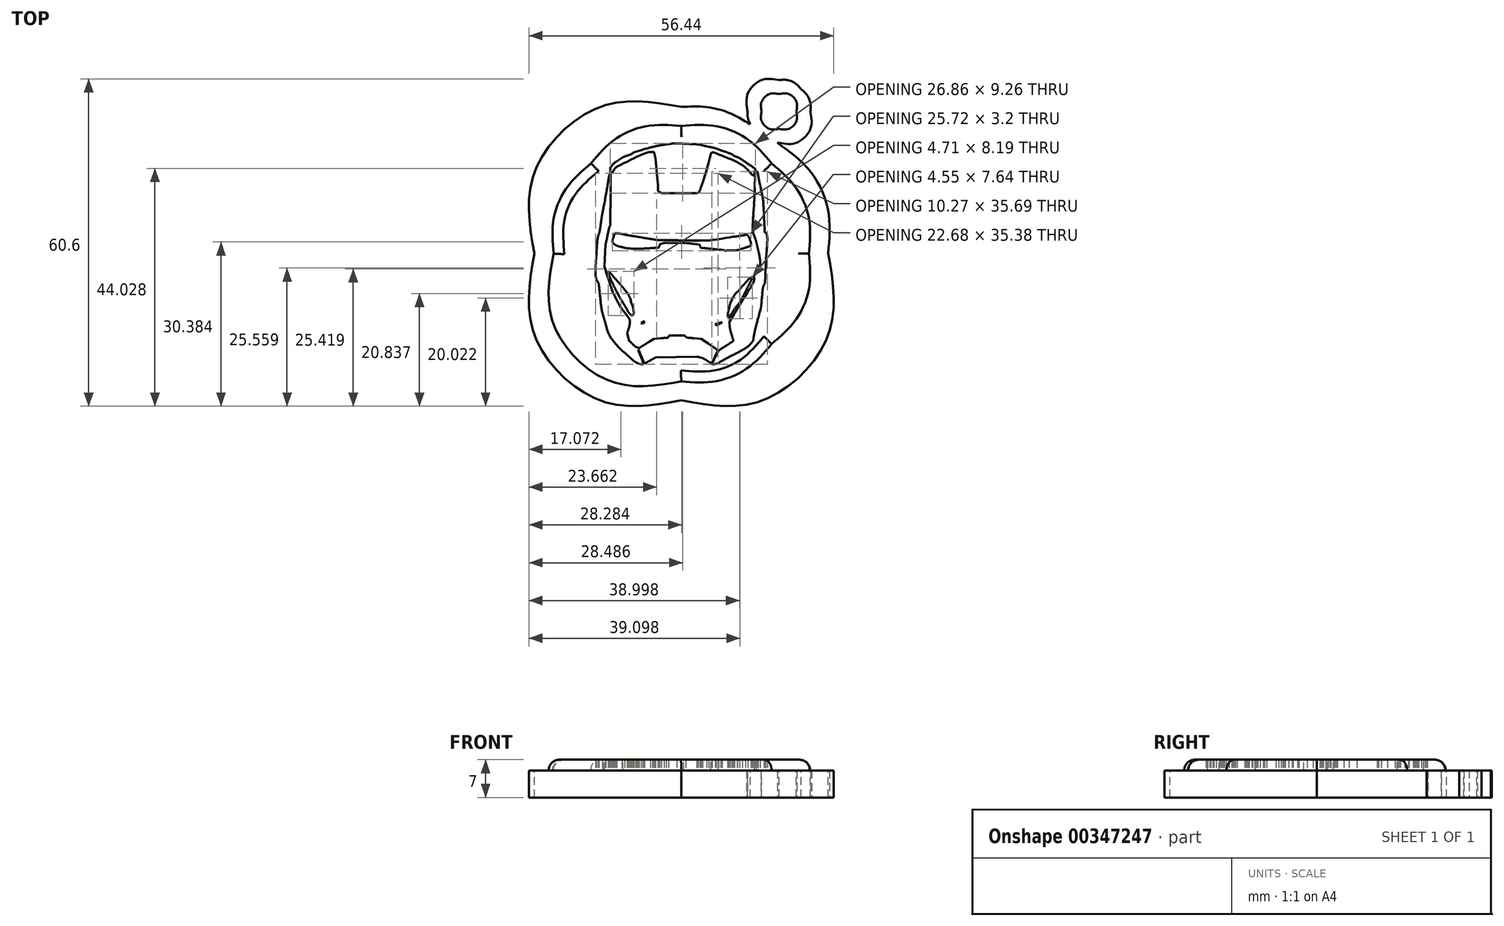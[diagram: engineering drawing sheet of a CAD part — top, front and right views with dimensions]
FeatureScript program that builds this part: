
annotation { "Feature Type Name" : "Feature", "Feature Type Description" : "" }
export const myFeature = defineFeature(function(context is Context, id is Id, definition is map)
    precondition{}
    {
        {
            var Q0;
            Q0=qCreatedBy(makeId("Top.planeOp"),FACE);
            var sketch = newSketch(context, id + "F0", { "sketchPlane" : qUnion([Q0])});
            skFitSpline(sketch, "E0", {"points": [v(-8.22, -22.7) * mm, v(-8.43, -22.6) * mm, v(-8.77, -22.38) * mm, v(-8.96, -22.21) * mm]});
            skFitSpline(sketch, "E1", {"points": [v(-8.96, -22.21) * mm, v(-9.15, -22.04) * mm, v(-9.54, -21.69) * mm, v(-9.83, -21.43) * mm]});
            skFitSpline(sketch, "E2", {"points": [v(-9.83, -21.43) * mm, v(-10.12, -21.17) * mm, v(-10.56, -20.8) * mm, v(-10.8, -20.6) * mm]});
            skFitSpline(sketch, "E3", {"points": [v(-10.8, -20.6) * mm, v(-11.06, -20.39) * mm, v(-11.61, -19.8) * mm, v(-12.04, -19.27) * mm]});
            skFitSpline(sketch, "E4", {"points": [v(-12.04, -19.27) * mm, v(-12.95, -18.16) * mm, v(-13.6, -16.93) * mm, v(-14, -15.53) * mm]});
            skFitSpline(sketch, "E5", {"points": [v(-14, -15.53) * mm, v(-14.14, -15.02) * mm, v(-14.36, -14.26) * mm, v(-14.48, -13.85) * mm]});
            skFitSpline(sketch, "E6", {"points": [v(-14.48, -13.85) * mm, v(-14.7, -13.05) * mm, v(-14.91, -11.53) * mm, v(-15.21, -8.5) * mm]});
            skFitSpline(sketch, "E7", {"points": [v(-15.21, -8.5) * mm, v(-15.23, -8.29) * mm, v(-15.34, -7.94) * mm, v(-15.45, -7.72) * mm]});
            skFitSpline(sketch, "E8", {"points": [v(-15.45, -7.72) * mm, v(-15.78, -7.08) * mm, v(-15.89, -5.4) * mm, v(-15.75, -3.2) * mm]});
            skFitSpline(sketch, "E9", {"points": [v(-15.75, -3.2) * mm, v(-15.59, -0.63) * mm, v(-15.46, 0.49) * mm, v(-15.26, 1.13) * mm]});
            skFitSpline(sketch, "E10", {"points": [v(-15.26, 1.13) * mm, v(-15.16, 1.44) * mm, v(-15, 2.32) * mm, v(-14.9, 3.1) * mm]});
            skFitSpline(sketch, "E11", {"points": [v(-14.9, 3.1) * mm, v(-14.79, 3.87) * mm, v(-14.66, 4.7) * mm, v(-14.6, 4.97) * mm]});
            skFitSpline(sketch, "E12", {"points": [v(-14.6, 4.97) * mm, v(-14.26, 6.74) * mm, v(-13.74, 9.57) * mm, v(-13.58, 10.63) * mm]});
            skFitSpline(sketch, "E13", {"points": [v(-13.58, 10.63) * mm, v(-13.47, 11.32) * mm, v(-13.35, 11.95) * mm, v(-13.32, 12.02) * mm]});
            skFitSpline(sketch, "E14", {"points": [v(-13.32, 12.02) * mm, v(-13.1, 12.44) * mm, v(-13.07, 11.84) * mm, v(-13.1, 7.5) * mm]});
            skFitSpline(sketch, "E15", {"points": [v(-13.1, 7.5) * mm, v(-13.12, 3.82) * mm, v(-13.16, 2.84) * mm, v(-13.27, 2.54) * mm]});
            skFitSpline(sketch, "E16", {"points": [v(-13.27, 2.54) * mm, v(-13.34, 2.33) * mm, v(-13.67, 0.81) * mm, v(-14, -0.83) * mm]});
            skFitSpline(sketch, "E17", {"points": [v(-14.24, -4.9) * mm, v(-14.04, -5.5) * mm, v(-13.61, -6.79) * mm, v(-13.3, -7.76) * mm]});
            skFitSpline(sketch, "E18", {"points": [v(-13.3, -7.76) * mm, v(-12.98, -8.74) * mm, v(-12.6, -9.77) * mm, v(-12.46, -10.06) * mm]});
            skFitSpline(sketch, "E19", {"points": [v(-12.46, -10.06) * mm, v(-11.7, -11.55) * mm, v(-11.06, -12.63) * mm, v(-10.45, -13.43) * mm]});
            skFitSpline(sketch, "E20", {"points": [v(-10.45, -13.43) * mm, v(-10.08, -13.92) * mm, v(-9.73, -14.4) * mm, v(-9.68, -14.5) * mm]});
            skFitSpline(sketch, "E21", {"points": [v(-9.68, -14.5) * mm, v(-9.52, -14.81) * mm, v(-9.71, -16.27) * mm, v(-10.03, -17.2) * mm]});
            skLineSegment(sketch, "E22", {"start": v(-14, -0.83) * mm, "end": v(-14.6, -3.82) * mm});
            skLineSegment(sketch, "E23", {"start": v(-14.6, -3.82) * mm, "end": v(-14.24, -4.9) * mm});
            skLineSegment(sketch, "E24", {"start": v(-14.24, -4.9) * mm, "end": v(-14, -0.83) * mm});
            skFitSpline(sketch, "E25", {"points": [v(-9.63, -18.65) * mm, v(-9.26, -19) * mm, v(-8.73, -19.48) * mm, v(-8.47, -19.74) * mm]});
            skLineSegment(sketch, "E26", {"start": v(-10.03, -17.2) * mm, "end": v(-10.32, -18.03) * mm});
            skLineSegment(sketch, "E27", {"start": v(-10.32, -18.03) * mm, "end": v(-9.63, -18.65) * mm});
            skLineSegment(sketch, "E28", {"start": v(-9.63, -18.65) * mm, "end": v(-10.03, -17.2) * mm});
            skFitSpline(sketch, "E29", {"points": [v(-7.78, -20) * mm, v(-7.66, -19.89) * mm, v(-7.37, -19.68) * mm, v(-7.13, -19.54) * mm]});
            skFitSpline(sketch, "E30", {"points": [v(-7.13, -19.54) * mm, v(-6.9, -19.4) * mm, v(-6.34, -19.06) * mm, v(-5.9, -18.78) * mm]});
            skLineSegment(sketch, "E31", {"start": v(-8.47, -19.74) * mm, "end": v(-8, -20.21) * mm});
            skLineSegment(sketch, "E32", {"start": v(-8, -20.21) * mm, "end": v(-7.78, -20) * mm});
            skLineSegment(sketch, "E33", {"start": v(-7.78, -20) * mm, "end": v(-8.47, -19.74) * mm});
            skFitSpline(sketch, "E34", {"points": [v(-3.8, -18.16) * mm, v(-2.63, -18.07) * mm, v(-2.5, -18.04) * mm, v(-2.37, -17.85) * mm]});
            skFitSpline(sketch, "E35", {"points": [v(-2.37, -17.85) * mm, v(-2.24, -17.65) * mm, v(-2.17, -17.64) * mm, v(-0.82, -17.64) * mm]});
            skFitSpline(sketch, "E36", {"points": [v(-0.82, -17.64) * mm, v(0.48, -17.64) * mm, v(0.6, -17.66) * mm, v(0.8, -17.84) * mm]});
            skFitSpline(sketch, "E37", {"points": [v(0.8, -17.84) * mm, v(0.97, -18) * mm, v(1.21, -18.05) * mm, v(2.35, -18.14) * mm]});
            skLineSegment(sketch, "E38", {"start": v(-5.9, -18.78) * mm, "end": v(-5.11, -18.26) * mm});
            skLineSegment(sketch, "E39", {"start": v(-5.11, -18.26) * mm, "end": v(-3.8, -18.16) * mm});
            skLineSegment(sketch, "E40", {"start": v(-3.8, -18.16) * mm, "end": v(-5.9, -18.78) * mm});
            skFitSpline(sketch, "E41", {"points": [v(4.95, -19.12) * mm, v(5.65, -19.59) * mm, v(6.34, -20.08) * mm, v(6.5, -20.2) * mm]});
            skLineSegment(sketch, "E42", {"start": v(2.35, -18.14) * mm, "end": v(3.7, -18.26) * mm});
            skLineSegment(sketch, "E43", {"start": v(3.7, -18.26) * mm, "end": v(4.95, -19.12) * mm});
            skLineSegment(sketch, "E44", {"start": v(4.95, -19.12) * mm, "end": v(2.35, -18.14) * mm});
            skFitSpline(sketch, "E45", {"points": [v(6.24, -21.52) * mm, v(5.94, -22.12) * mm, v(5.63, -22.63) * mm, v(5.56, -22.66) * mm]});
            skFitSpline(sketch, "E46", {"points": [v(5.56, -22.66) * mm, v(5.49, -22.7) * mm, v(5.1, -22.51) * mm, v(4.7, -22.27) * mm]});
            skFitSpline(sketch, "E47", {"points": [v(4.7, -22.27) * mm, v(4.13, -21.93) * mm, v(3.73, -21.77) * mm, v(2.85, -21.55) * mm]});
            skLineSegment(sketch, "E48", {"start": v(6.5, -20.2) * mm, "end": v(6.78, -20.43) * mm});
            skLineSegment(sketch, "E49", {"start": v(6.78, -20.43) * mm, "end": v(6.24, -21.52) * mm});
            skLineSegment(sketch, "E50", {"start": v(6.24, -21.52) * mm, "end": v(6.5, -20.2) * mm});
            skFitSpline(sketch, "E51", {"points": [v(-4.73, -21.7) * mm, v(-5.04, -21.87) * mm, v(-5.61, -22.18) * mm, v(-6, -22.4) * mm]});
            skFitSpline(sketch, "E52", {"points": [v(-6, -22.4) * mm, v(-6.38, -22.6) * mm, v(-6.74, -22.75) * mm, v(-6.8, -22.71) * mm]});
            skFitSpline(sketch, "E53", {"points": [v(-6.8, -22.71) * mm, v(-6.85, -22.68) * mm, v(-7, -22.42) * mm, v(-7.11, -22.13) * mm]});
            skFitSpline(sketch, "E54", {"points": [v(-7.11, -22.13) * mm, v(-7.53, -21.14) * mm, v(-7.9, -20.35) * mm, v(-7.93, -20.39) * mm]});
            skFitSpline(sketch, "E55", {"points": [v(-7.93, -20.39) * mm, v(-7.95, -20.4) * mm, v(-7.76, -20.94) * mm, v(-7.5, -21.57) * mm]});
            skFitSpline(sketch, "E56", {"points": [v(-7.5, -21.57) * mm, v(-7.24, -22.2) * mm, v(-7.03, -22.76) * mm, v(-7.03, -22.8) * mm]});
            skFitSpline(sketch, "E57", {"points": [v(-7.03, -22.8) * mm, v(-7.03, -22.95) * mm, v(-7.81, -22.88) * mm, v(-8.22, -22.7) * mm]});
            skLineSegment(sketch, "E58", {"start": v(2.85, -21.55) * mm, "end": v(1.73, -21.27) * mm});
            skLineSegment(sketch, "E59", {"start": v(1.73, -21.27) * mm, "end": v(-1.22, -21.34) * mm});
            skLineSegment(sketch, "E60", {"start": v(-1.22, -21.34) * mm, "end": v(-4.17, -21.4) * mm});
            skLineSegment(sketch, "E61", {"start": v(-4.17, -21.4) * mm, "end": v(-4.73, -21.7) * mm});
            skLineSegment(sketch, "E62", {"start": v(-4.73, -21.7) * mm, "end": v(2.85, -21.55) * mm});
            skFitSpline(sketch, "E63", {"points": [v(5.72, -22.81) * mm, v(5.88, -22.45) * mm, v(6.87, -20.56) * mm, v(6.95, -20.44) * mm]});
            skFitSpline(sketch, "E64", {"points": [v(6.95, -20.44) * mm, v(7.01, -20.37) * mm, v(7.59, -19.97) * mm, v(8.23, -19.56) * mm]});
            skFitSpline(sketch, "E65", {"points": [v(8.23, -19.56) * mm, v(8.87, -19.16) * mm, v(9.46, -18.77) * mm, v(9.52, -18.71) * mm]});
            skFitSpline(sketch, "E66", {"points": [v(9.52, -18.71) * mm, v(9.63, -18.62) * mm, v(9.6, -18.41) * mm, v(9.33, -17.54) * mm]});
            skFitSpline(sketch, "E67", {"points": [v(9.33, -17.54) * mm, v(9.15, -16.95) * mm, v(8.98, -16.17) * mm, v(8.95, -15.8) * mm]});
            skFitSpline(sketch, "E68", {"points": [v(9.78, -13.67) * mm, v(10.27, -12.85) * mm, v(11, -11.68) * mm, v(11.39, -11.05) * mm]});
            skFitSpline(sketch, "E69", {"points": [v(11.39, -11.05) * mm, v(12.53, -9.23) * mm, v(13.47, -7.38) * mm, v(13.47, -6.95) * mm]});
            skFitSpline(sketch, "E70", {"points": [v(13.47, -6.95) * mm, v(13.47, -6.67) * mm, v(13.61, -6.33) * mm, v(14.03, -5.57) * mm]});
            skFitSpline(sketch, "E71", {"points": [v(14.03, -5.57) * mm, v(14.42, -4.87) * mm, v(14.6, -4.46) * mm, v(14.6, -4.23) * mm]});
            skFitSpline(sketch, "E72", {"points": [v(14.6, -4.23) * mm, v(14.6, -3.9) * mm, v(14.38, -2.52) * mm, v(14.23, -1.87) * mm]});
            skFitSpline(sketch, "E73", {"points": [v(14.23, -1.87) * mm, v(14.18, -1.66) * mm, v(14.07, -1.18) * mm, v(13.98, -0.8) * mm]});
            skFitSpline(sketch, "E74", {"points": [v(13.98, -0.8) * mm, v(13.9, -0.4) * mm, v(13.72, 0.2) * mm, v(13.6, 0.57) * mm]});
            skFitSpline(sketch, "E75", {"points": [v(13.6, 0.57) * mm, v(13.27, 1.49) * mm, v(13.23, 2.84) * mm, v(13.43, 6.28) * mm]});
            skFitSpline(sketch, "E76", {"points": [v(13.43, 6.28) * mm, v(13.52, 7.82) * mm, v(13.6, 9.76) * mm, v(13.62, 10.58) * mm]});
            skFitSpline(sketch, "E77", {"points": [v(13.62, 10.58) * mm, v(13.64, 12.14) * mm, v(13.72, 12.62) * mm, v(13.95, 12.67) * mm]});
            skFitSpline(sketch, "E78", {"points": [v(13.95, 12.67) * mm, v(14.06, 12.69) * mm, v(14.2, 12.19) * mm, v(14.58, 10.23) * mm]});
            skFitSpline(sketch, "E79", {"points": [v(14.58, 10.23) * mm, v(15.08, 7.68) * mm, v(15.18, 6.84) * mm, v(15.35, 3.47) * mm]});
            skFitSpline(sketch, "E80", {"points": [v(15.35, 3.47) * mm, v(15.43, 1.84) * mm, v(15.47, 1.48) * mm, v(15.6, 1.33) * mm]});
            skFitSpline(sketch, "E81", {"points": [v(15.6, 1.33) * mm, v(15.82, 1.1) * mm, v(15.87, -0.9) * mm, v(15.72, -3) * mm]});
            skFitSpline(sketch, "E82", {"points": [v(15.72, -3) * mm, v(15.66, -3.81) * mm, v(15.6, -5.25) * mm, v(15.56, -6.17) * mm]});
            skFitSpline(sketch, "E83", {"points": [v(15.56, -6.17) * mm, v(15.51, -7.63) * mm, v(15.48, -7.91) * mm, v(15.3, -8.32) * mm]});
            skFitSpline(sketch, "E84", {"points": [v(15.3, -8.32) * mm, v(15.14, -8.69) * mm, v(15.05, -9.2) * mm, v(14.93, -10.53) * mm]});
            skFitSpline(sketch, "E85", {"points": [v(14.93, -10.53) * mm, v(14.77, -12.27) * mm, v(14.72, -12.52) * mm, v(14.27, -14.22) * mm]});
            skFitSpline(sketch, "E86", {"points": [v(14.27, -14.22) * mm, v(13.86, -15.73) * mm, v(13.58, -16.96) * mm, v(13.37, -18.1) * mm]});
            skFitSpline(sketch, "E87", {"points": [v(13.37, -18.1) * mm, v(13.29, -18.53) * mm, v(13.18, -18.79) * mm, v(12.98, -19.01) * mm]});
            skFitSpline(sketch, "E88", {"points": [v(12.98, -19.01) * mm, v(12.59, -19.46) * mm, v(11.16, -20.41) * mm, v(9.85, -21.1) * mm]});
            skFitSpline(sketch, "E89", {"points": [v(9.85, -21.1) * mm, v(9.24, -21.43) * mm, v(8.4, -21.87) * mm, v(8, -22.09) * mm]});
            skFitSpline(sketch, "E90", {"points": [v(8, -22.09) * mm, v(7.59, -22.3) * mm, v(7.08, -22.58) * mm, v(6.88, -22.69) * mm]});
            skFitSpline(sketch, "E91", {"points": [v(6.88, -22.69) * mm, v(6.52, -22.87) * mm, v(5.65, -22.97) * mm, v(5.72, -22.81) * mm]});
            skLineSegment(sketch, "E92", {"start": v(8.95, -15.8) * mm, "end": v(8.89, -15.14) * mm});
            skLineSegment(sketch, "E93", {"start": v(8.89, -15.14) * mm, "end": v(9.78, -13.67) * mm});
            skLineSegment(sketch, "E94", {"start": v(9.78, -13.67) * mm, "end": v(8.95, -15.8) * mm});
            skFitSpline(sketch, "E95", {"points": [v(5.7, -16.17) * mm, v(5.41, -15.87) * mm, v(5.07, -15.49) * mm, v(4.93, -15.31) * mm]});
            skFitSpline(sketch, "E96", {"points": [v(4.93, -15.31) * mm, v(4.77, -15.12) * mm, v(4.53, -14.96) * mm, v(4.32, -14.91) * mm]});
            skFitSpline(sketch, "E97", {"points": [v(4.32, -14.91) * mm, v(3.86, -14.8) * mm, v(-4.6, -14.64) * mm, v(-5.04, -14.74) * mm]});
            skFitSpline(sketch, "E98", {"points": [v(-5.04, -14.74) * mm, v(-5.31, -14.8) * mm, v(-5.55, -15) * mm, v(-6.17, -15.67) * mm]});
            skFitSpline(sketch, "E99", {"points": [v(-6.17, -15.67) * mm, v(-6.6, -16.14) * mm, v(-7.02, -16.52) * mm, v(-7.1, -16.52) * mm]});
            skFitSpline(sketch, "E100", {"points": [v(-7.1, -16.52) * mm, v(-7.2, -16.52) * mm, v(-7.6, -16.24) * mm, v(-8.01, -15.9) * mm]});
            skFitSpline(sketch, "E101", {"points": [v(-8.01, -15.9) * mm, v(-9.43, -14.71) * mm, v(-9.39, -14.76) * mm, v(-9.32, -14.45) * mm]});
            skFitSpline(sketch, "E102", {"points": [v(-9.32, -14.45) * mm, v(-9.28, -14.3) * mm, v(-9.2, -14.14) * mm, v(-9.12, -14.11) * mm]});
            skFitSpline(sketch, "E103", {"points": [v(-9.12, -14.11) * mm, v(-9.05, -14.08) * mm, v(-8.72, -14.28) * mm, v(-8.36, -14.57) * mm]});
            skFitSpline(sketch, "E104", {"points": [v(-8.36, -14.57) * mm, v(-8.01, -14.85) * mm, v(-7.6, -15.17) * mm, v(-7.43, -15.28) * mm]});
            skFitSpline(sketch, "E105", {"points": [v(-6.77, -15) * mm, v(-6.57, -14.73) * mm, v(-6.34, -14.39) * mm, v(-6.25, -14.25) * mm]});
            skFitSpline(sketch, "E106", {"points": [v(-6.25, -14.25) * mm, v(-5.88, -13.66) * mm, v(-6.02, -13.68) * mm, v(-1.47, -13.7) * mm]});
            skFitSpline(sketch, "E107", {"points": [v(-1.47, -13.7) * mm, v(2.96, -13.7) * mm, v(4.58, -13.76) * mm, v(4.95, -13.9) * mm]});
            skFitSpline(sketch, "E108", {"points": [v(4.95, -13.9) * mm, v(5.08, -13.96) * mm, v(5.39, -14.28) * mm, v(5.63, -14.63) * mm]});
            skFitSpline(sketch, "E109", {"points": [v(5.63, -14.63) * mm, v(5.88, -14.97) * mm, v(6.17, -15.37) * mm, v(6.29, -15.51) * mm]});
            skLineSegment(sketch, "E110", {"start": v(-7.43, -15.28) * mm, "end": v(-7.13, -15.5) * mm});
            skLineSegment(sketch, "E111", {"start": v(-7.13, -15.5) * mm, "end": v(-6.77, -15) * mm});
            skLineSegment(sketch, "E112", {"start": v(-6.77, -15) * mm, "end": v(-7.43, -15.28) * mm});
            skFitSpline(sketch, "E113", {"points": [v(7.53, -15.16) * mm, v(8.1, -14.83) * mm, v(8.61, -14.55) * mm, v(8.68, -14.55) * mm]});
            skFitSpline(sketch, "E114", {"points": [v(8.68, -14.55) * mm, v(8.76, -14.55) * mm, v(8.8, -14.65) * mm, v(8.78, -14.85) * mm]});
            skFitSpline(sketch, "E115", {"points": [v(8.78, -14.85) * mm, v(8.75, -15.1) * mm, v(8.62, -15.23) * mm, v(7.63, -15.92) * mm]});
            skFitSpline(sketch, "E116", {"points": [v(7.63, -15.92) * mm, v(7.01, -16.35) * mm, v(6.44, -16.7) * mm, v(6.35, -16.7) * mm]});
            skFitSpline(sketch, "E117", {"points": [v(6.35, -16.7) * mm, v(6.27, -16.7) * mm, v(5.97, -16.46) * mm, v(5.7, -16.17) * mm]});
            skLineSegment(sketch, "E118", {"start": v(6.29, -15.51) * mm, "end": v(6.5, -15.77) * mm});
            skLineSegment(sketch, "E119", {"start": v(6.5, -15.77) * mm, "end": v(7.53, -15.16) * mm});
            skLineSegment(sketch, "E120", {"start": v(7.53, -15.16) * mm, "end": v(6.29, -15.51) * mm});
            skFitSpline(sketch, "E121", {"points": [v(8.72, -14.34) * mm, v(8.62, -14.21) * mm, v(8.72, -13.1) * mm, v(8.9, -12.4) * mm]});
            skFitSpline(sketch, "E122", {"points": [v(8.9, -12.4) * mm, v(9.1, -11.62) * mm, v(10.02, -9.88) * mm, v(10.42, -9.54) * mm]});
            skFitSpline(sketch, "E123", {"points": [v(10.42, -9.54) * mm, v(10.48, -9.5) * mm, v(10.65, -9.3) * mm, v(10.8, -9.12) * mm]});
            skFitSpline(sketch, "E124", {"points": [v(10.8, -9.12) * mm, v(11.44, -8.33) * mm, v(12.94, -6.87) * mm, v(13.06, -6.91) * mm]});
            skFitSpline(sketch, "E125", {"points": [v(13.06, -6.91) * mm, v(13.15, -6.95) * mm, v(13.03, -7.25) * mm, v(12.62, -8.06) * mm]});
            skFitSpline(sketch, "E126", {"points": [v(12.62, -8.06) * mm, v(11.48, -10.26) * mm, v(10.72, -11.61) * mm, v(10.34, -12.12) * mm]});
            skFitSpline(sketch, "E127", {"points": [v(10.34, -12.12) * mm, v(9.88, -12.72) * mm, v(8.98, -14.2) * mm, v(8.98, -14.35) * mm]});
            skFitSpline(sketch, "E128", {"points": [v(8.98, -14.35) * mm, v(8.98, -14.5) * mm, v(8.84, -14.49) * mm, v(8.72, -14.34) * mm]});
            skFitSpline(sketch, "E129", {"points": [v(-9.47, -13.68) * mm, v(-9.64, -13.5) * mm, v(-9.87, -13.2) * mm, v(-9.97, -13) * mm]});
            skFitSpline(sketch, "E130", {"points": [v(-9.97, -13) * mm, v(-10.07, -12.8) * mm, v(-10.53, -12) * mm, v(-11, -11.23) * mm]});
            skFitSpline(sketch, "E131", {"points": [v(-11, -11.23) * mm, v(-11.46, -10.46) * mm, v(-12.05, -9.36) * mm, v(-12.33, -8.8) * mm]});
            skFitSpline(sketch, "E132", {"points": [v(-12.33, -8.8) * mm, v(-12.83, -7.74) * mm, v(-13.49, -6.17) * mm, v(-13.49, -6.01) * mm]});
            skFitSpline(sketch, "E133", {"points": [v(-13.49, -6.01) * mm, v(-13.49, -5.78) * mm, v(-13.14, -6.08) * mm, v(-12.3, -7.06) * mm]});
            skFitSpline(sketch, "E134", {"points": [v(-12.3, -7.06) * mm, v(-10.33, -9.34) * mm, v(-9.62, -10.41) * mm, v(-9.18, -11.74) * mm]});
            skFitSpline(sketch, "E135", {"points": [v(-9.18, -11.74) * mm, v(-8.92, -12.56) * mm, v(-8.82, -13.72) * mm, v(-9.01, -13.87) * mm]});
            skFitSpline(sketch, "E136", {"points": [v(-9.01, -13.87) * mm, v(-9.13, -13.97) * mm, v(-9.2, -13.93) * mm, v(-9.47, -13.68) * mm]});
            skFitSpline(sketch, "E137", {"points": [v(7.95, -1.88) * mm, v(7.92, -1.86) * mm, v(7.02, -1.75) * mm, v(5.94, -1.64) * mm]});
            skFitSpline(sketch, "E138", {"points": [v(5.94, -1.64) * mm, v(3.79, -1.42) * mm, v(3.58, -1.35) * mm, v(3.41, -0.8) * mm]});
            skFitSpline(sketch, "E139", {"points": [v(0.42, -0.5) * mm, v(-1.18, -0.49) * mm, v(-2.8, -0.47) * mm, v(-3.18, -0.47) * mm]});
            skLineSegment(sketch, "E140", {"start": v(3.41, -0.8) * mm, "end": v(3.32, -0.51) * mm});
            skLineSegment(sketch, "E141", {"start": v(3.32, -0.51) * mm, "end": v(0.42, -0.5) * mm});
            skLineSegment(sketch, "E142", {"start": v(0.42, -0.5) * mm, "end": v(3.41, -0.8) * mm});
            skFitSpline(sketch, "E143", {"points": [v(-3.98, -0.76) * mm, v(-4.17, -1.33) * mm, v(-4.27, -1.37) * mm, v(-5.73, -1.46) * mm]});
            skFitSpline(sketch, "E144", {"points": [v(-5.73, -1.46) * mm, v(-7.53, -1.57) * mm, v(-10.06, -1.47) * mm, v(-10.98, -1.26) * mm]});
            skFitSpline(sketch, "E145", {"points": [v(-10.98, -1.26) * mm, v(-11.64, -1.11) * mm, v(-12.47, -0.7) * mm, v(-12.72, -0.39) * mm]});
            skFitSpline(sketch, "E146", {"points": [v(-12.72, -0.39) * mm, v(-12.79, -0.3) * mm, v(-12.74, -0.04) * mm, v(-12.57, 0.5) * mm]});
            skLineSegment(sketch, "E147", {"start": v(-3.18, -0.47) * mm, "end": v(-3.87, -0.46) * mm});
            skLineSegment(sketch, "E148", {"start": v(-3.87, -0.46) * mm, "end": v(-3.98, -0.76) * mm});
            skLineSegment(sketch, "E149", {"start": v(-3.98, -0.76) * mm, "end": v(-3.18, -0.47) * mm});
            skFitSpline(sketch, "E150", {"points": [v(-11.92, 1.27) * mm, v(-11.7, 1.27) * mm, v(-11.13, 1.19) * mm, v(-10.65, 1.09) * mm]});
            skFitSpline(sketch, "E151", {"points": [v(-10.65, 1.09) * mm, v(-9.79, 0.9) * mm, v(-9.34, 0.83) * mm, v(-6.51, 0.38) * mm]});
            skFitSpline(sketch, "E152", {"points": [v(-6.51, 0.38) * mm, v(-5.69, 0.24) * mm, v(-4.9, 0.11) * mm, v(-4.78, 0.09) * mm]});
            skFitSpline(sketch, "E153", {"points": [v(-4.78, 0.09) * mm, v(-4.65, 0.06) * mm, v(-2.78, 0.02) * mm, v(-0.63, -0.01) * mm]});
            skFitSpline(sketch, "E154", {"points": [v(-0.63, -0.01) * mm, v(3.84, -0.08) * mm, v(5.67, 0.04) * mm, v(9.5, 0.62) * mm]});
            skFitSpline(sketch, "E155", {"points": [v(9.5, 0.62) * mm, v(12, 1) * mm, v(12.17, 1.02) * mm, v(12.3, 0.88) * mm]});
            skFitSpline(sketch, "E156", {"points": [v(12.3, 0.88) * mm, v(12.41, 0.77) * mm, v(12.91, -0.62) * mm, v(12.91, -0.81) * mm]});
            skFitSpline(sketch, "E157", {"points": [v(12.91, -0.81) * mm, v(12.91, -0.93) * mm, v(12.19, -1.26) * mm, v(11.28, -1.57) * mm]});
            skFitSpline(sketch, "E158", {"points": [v(11.28, -1.57) * mm, v(10.55, -1.8) * mm, v(10.26, -1.86) * mm, v(9.21, -1.9) * mm]});
            skFitSpline(sketch, "E159", {"points": [v(9.21, -1.9) * mm, v(8.54, -1.91) * mm, v(7.98, -1.9) * mm, v(7.95, -1.88) * mm]});
            skLineSegment(sketch, "E160", {"start": v(-12.57, 0.5) * mm, "end": v(-12.32, 1.27) * mm});
            skLineSegment(sketch, "E161", {"start": v(-12.32, 1.27) * mm, "end": v(-11.92, 1.27) * mm});
            skLineSegment(sketch, "E162", {"start": v(-11.92, 1.27) * mm, "end": v(-12.57, 0.5) * mm});
            skFitSpline(sketch, "E163", {"points": [v(-3.66, 8.74) * mm, v(-3.73, 8.76) * mm, v(-3.91, 8.86) * mm, v(-4.05, 8.96) * mm]});
            skFitSpline(sketch, "E164", {"points": [v(-4.05, 8.96) * mm, v(-4.29, 9.13) * mm, v(-4.31, 9.2) * mm, v(-4.31, 9.7) * mm]});
            skFitSpline(sketch, "E165", {"points": [v(-4.31, 9.7) * mm, v(-4.31, 10.02) * mm, v(-4.35, 10.66) * mm, v(-4.4, 11.13) * mm]});
            skFitSpline(sketch, "E166", {"points": [v(-4.4, 11.13) * mm, v(-4.45, 11.6) * mm, v(-4.54, 12.51) * mm, v(-4.6, 13.16) * mm]});
            skFitSpline(sketch, "E167", {"points": [v(-4.6, 13.16) * mm, v(-4.72, 14.56) * mm, v(-4.85, 15.51) * mm, v(-4.97, 15.99) * mm]});
            skFitSpline(sketch, "E168", {"points": [v(-4.97, 15.99) * mm, v(-5.06, 16.3) * mm, v(-5.1, 16.34) * mm, v(-5.34, 16.34) * mm]});
            skFitSpline(sketch, "E169", {"points": [v(-5.34, 16.34) * mm, v(-5.88, 16.34) * mm, v(-8.3, 15.43) * mm, v(-9.97, 14.59) * mm]});
            skFitSpline(sketch, "E170", {"points": [v(-9.97, 14.59) * mm, v(-11.42, 13.87) * mm, v(-12.25, 13.33) * mm, v(-12.5, 12.96) * mm]});
            skFitSpline(sketch, "E171", {"points": [v(-12.5, 12.96) * mm, v(-12.85, 12.46) * mm, v(-13.08, 12.47) * mm, v(-13.13, 13) * mm]});
            skFitSpline(sketch, "E172", {"points": [v(-13.13, 13) * mm, v(-13.16, 13.34) * mm, v(-13.13, 13.44) * mm, v(-12.84, 13.8) * mm]});
            skFitSpline(sketch, "E173", {"points": [v(-12.84, 13.8) * mm, v(-12.46, 14.25) * mm, v(-10.5, 15.5) * mm, v(-9.78, 15.75) * mm]});
            skFitSpline(sketch, "E174", {"points": [v(-9.78, 15.75) * mm, v(-9.53, 15.83) * mm, v(-9.24, 15.95) * mm, v(-9.13, 16.02) * mm]});
            skFitSpline(sketch, "E175", {"points": [v(-9.13, 16.02) * mm, v(-8.86, 16.19) * mm, v(-6.54, 16.95) * mm, v(-5.32, 17.26) * mm]});
            skFitSpline(sketch, "E176", {"points": [v(-5.32, 17.26) * mm, v(-4.74, 17.42) * mm, v(-3.6, 17.63) * mm, v(-2.77, 17.74) * mm]});
            skFitSpline(sketch, "E177", {"points": [v(-2.77, 17.74) * mm, v(-1.37, 17.94) * mm, v(-1.12, 17.94) * mm, v(0.93, 17.85) * mm]});
            skFitSpline(sketch, "E178", {"points": [v(0.93, 17.85) * mm, v(2.5, 17.79) * mm, v(3.36, 17.7) * mm, v(3.93, 17.58) * mm]});
            skFitSpline(sketch, "E179", {"points": [v(3.93, 17.58) * mm, v(4.36, 17.47) * mm, v(5.06, 17.32) * mm, v(5.47, 17.23) * mm]});
            skFitSpline(sketch, "E180", {"points": [v(5.47, 17.23) * mm, v(5.88, 17.14) * mm, v(6.5, 16.97) * mm, v(6.83, 16.85) * mm]});
            skFitSpline(sketch, "E181", {"points": [v(6.83, 16.85) * mm, v(8.6, 16.21) * mm, v(9.51, 15.82) * mm, v(9.68, 15.63) * mm]});
            skFitSpline(sketch, "E182", {"points": [v(10.27, 15.38) * mm, v(10.54, 15.34) * mm, v(11.02, 15.06) * mm, v(11.85, 14.48) * mm]});
            skFitSpline(sketch, "E183", {"points": [v(11.85, 14.48) * mm, v(13.28, 13.52) * mm, v(13.7, 13.13) * mm, v(13.62, 12.84) * mm]});
            skFitSpline(sketch, "E184", {"points": [v(13.62, 12.84) * mm, v(13.59, 12.73) * mm, v(13.54, 12.53) * mm, v(13.5, 12.38) * mm]});
            skFitSpline(sketch, "E185", {"points": [v(13.5, 12.38) * mm, v(13.42, 12.01) * mm, v(13.2, 12.06) * mm, v(12.72, 12.56) * mm]});
            skFitSpline(sketch, "E186", {"points": [v(12.72, 12.56) * mm, v(11.7, 13.6) * mm, v(9.84, 14.7) * mm, v(7.3, 15.74) * mm]});
            skFitSpline(sketch, "E187", {"points": [v(7.3, 15.74) * mm, v(6.23, 16.17) * mm, v(5.81, 16.3) * mm, v(5.7, 16.24) * mm]});
            skFitSpline(sketch, "E188", {"points": [v(5.7, 16.24) * mm, v(5.51, 16.14) * mm, v(5.45, 15.96) * mm, v(5.1, 14.56) * mm]});
            skFitSpline(sketch, "E189", {"points": [v(5.1, 14.56) * mm, v(4.86, 13.61) * mm, v(3.93, 10.6) * mm, v(3.53, 9.48) * mm]});
            skFitSpline(sketch, "E190", {"points": [v(3.53, 9.48) * mm, v(3.42, 9.17) * mm, v(3.25, 8.89) * mm, v(3.14, 8.82) * mm]});
            skFitSpline(sketch, "E191", {"points": [v(3.14, 8.82) * mm, v(3, 8.74) * mm, v(2.04, 8.7) * mm, v(-0.29, 8.7) * mm]});
            skFitSpline(sketch, "E192", {"points": [v(-0.29, 8.7) * mm, v(-2.06, 8.7) * mm, v(-3.58, 8.71) * mm, v(-3.66, 8.74) * mm]});
            skFitSpline(sketch, "E193", {"points": [v(23.65, -2.5) * mm, v(23.65, -8.76) * mm, v(21.15, -14.78) * mm, v(16.72, -19.21) * mm]});
            skFitSpline(sketch, "E194", {"points": [v(16.72, -19.21) * mm, v(12.29, -23.64) * mm, v(6.27, -26.14) * mm, v(0, -26.14) * mm]});
            skFitSpline(sketch, "E195", {"points": [v(0, -26.14) * mm, v(-13.06, -26.14) * mm, v(-23.65, -15.55) * mm, v(-23.65, -2.5) * mm]});
            skFitSpline(sketch, "E196", {"points": [v(-23.65, -2.5) * mm, v(-23.65, 3.78) * mm, v(-21.15, 9.8) * mm, v(-16.72, 14.23) * mm]});
            skFitSpline(sketch, "E197", {"points": [v(-16.72, 14.23) * mm, v(-12.29, 18.66) * mm, v(-6.27, 21.16) * mm, v(0, 21.16) * mm]});
            skFitSpline(sketch, "E198", {"points": [v(0, 21.16) * mm, v(6.27, 21.16) * mm, v(12.29, 18.66) * mm, v(16.72, 14.23) * mm]});
            skFitSpline(sketch, "E199", {"points": [v(16.72, 14.23) * mm, v(21.15, 9.8) * mm, v(23.65, 3.78) * mm, v(23.65, -2.5) * mm]});
            skFitSpline(sketch, "E200", {"points": [v(18.08, 29.67) * mm, v(14.87, 29.67) * mm, v(12.26, 27.07) * mm, v(12.26, 23.85) * mm]});
            skFitSpline(sketch, "E201", {"points": [v(12.26, 23.85) * mm, v(12.27, 23.04) * mm, v(12.44, 22.23) * mm, v(12.78, 21.48) * mm]});
            skFitSpline(sketch, "E202", {"points": [v(12.78, 21.48) * mm, v(8.84, 23.58) * mm, v(4.46, 24.68) * mm, v(0, 24.69) * mm]});
            skFitSpline(sketch, "E203", {"points": [v(0, 24.69) * mm, v(-15.01, 24.69) * mm, v(-27.18, 12.52) * mm, v(-27.18, -2.5) * mm]});
            skFitSpline(sketch, "E204", {"points": [v(-27.18, -2.5) * mm, v(-27.18, -17.5) * mm, v(-15.01, -29.67) * mm, v(0, -29.67) * mm]});
            skFitSpline(sketch, "E205", {"points": [v(0, -29.67) * mm, v(15.01, -29.67) * mm, v(27.18, -17.5) * mm, v(27.18, -2.5) * mm]});
            skFitSpline(sketch, "E206", {"points": [v(27.18, -2.5) * mm, v(27.17, 5.4) * mm, v(23.74, 12.9) * mm, v(17.77, 18.05) * mm]});
            skFitSpline(sketch, "E207", {"points": [v(17.77, 18.05) * mm, v(17.87, 18.05) * mm, v(17.98, 18.04) * mm, v(18.08, 18.04) * mm]});
            skFitSpline(sketch, "E208", {"points": [v(18.08, 18.04) * mm, v(21.29, 18.04) * mm, v(23.9, 20.64) * mm, v(23.9, 23.85) * mm]});
            skFitSpline(sketch, "E209", {"points": [v(23.9, 23.85) * mm, v(23.9, 25.4) * mm, v(23.28, 26.88) * mm, v(22.2, 27.97) * mm]});
            skFitSpline(sketch, "E210", {"points": [v(22.2, 27.97) * mm, v(21.1, 29.06) * mm, v(19.62, 29.67) * mm, v(18.08, 29.67) * mm]});
            skFitSpline(sketch, "E211", {"points": [v(21.3, 23.85) * mm, v(21.3, 22.07) * mm, v(19.86, 20.63) * mm, v(18.08, 20.63) * mm]});
            skFitSpline(sketch, "E212", {"points": [v(18.08, 20.63) * mm, v(16.3, 20.63) * mm, v(14.85, 22.07) * mm, v(14.85, 23.85) * mm]});
            skFitSpline(sketch, "E213", {"points": [v(14.85, 23.85) * mm, v(14.85, 25.63) * mm, v(16.3, 27.08) * mm, v(18.08, 27.08) * mm]});
            skFitSpline(sketch, "E214", {"points": [v(18.08, 27.08) * mm, v(19.86, 27.08) * mm, v(21.3, 25.63) * mm, v(21.3, 23.85) * mm]});
            skArc(sketch, "E215", {"start": v(10.4, 15.35) * mm, "mid": v(10.05, 15.51) * mm, "end": v(9.68, 15.63) * mm});
            skSolve(sketch);
        }
        {
            var Q0;
            Q0=makeQuery(id+"F0.imprint","IMPRINT",FACE,{"disambiguationData":[TD([[makeQuery(id+"F0.imprint","IMPRINT",EDGE,{"derivedFrom":sQuery(id+"F0.wireOp",EDGE,"E0")}),1.0]])]});
            extrude(context, id + "F1", {"entities" : qUnion([Q0]), "depth" : 2 * mm});
        }
        {
            var Q0;
            Q0=makeQuery(id+"F1.opExtrude","CAP_EDGE",EDGE,{"disambiguationData":[OSD([sQuery(id+"F0.wireOp",EDGE,"E197")])],"isStart":false});
            var Q1;
            Q1=makeQuery(id+"F1.opExtrude","CAP_EDGE",EDGE,{"disambiguationData":[OSD([sQuery(id+"F0.wireOp",EDGE,"E198")])],"isStart":false});
            var Q2;
            Q2=makeQuery(id+"F1.opExtrude","CAP_EDGE",EDGE,{"disambiguationData":[OSD([sQuery(id+"F0.wireOp",EDGE,"E199")])],"isStart":false});
            var Q3;
            Q3=makeQuery(id+"F1.opExtrude","CAP_EDGE",EDGE,{"disambiguationData":[OSD([sQuery(id+"F0.wireOp",EDGE,"E193")])],"isStart":false});
            var Q4;
            Q4=makeQuery(id+"F1.opExtrude","CAP_EDGE",EDGE,{"disambiguationData":[OSD([sQuery(id+"F0.wireOp",EDGE,"E194")])],"isStart":false});
            var Q5;
            Q5=makeQuery(id+"F1.opExtrude","CAP_EDGE",EDGE,{"disambiguationData":[OSD([sQuery(id+"F0.wireOp",EDGE,"E195")])],"isStart":false});
            var Q6;
            Q6=makeQuery(id+"F1.opExtrude","CAP_EDGE",EDGE,{"disambiguationData":[OSD([sQuery(id+"F0.wireOp",EDGE,"E196")])],"isStart":false});
            fillet(context, id + "F2", {"entities" : qUnion([Q0, Q1, Q2, Q3, Q4, Q5, Q6]), "radius" : 2 * mm, "tangentPropagation" : true, "allowEdgeOverflow" : false});
        }
        {
            var Q0;
            Q0=makeQuery(id+"F0.imprint","IMPRINT",FACE,{"disambiguationData":[TD([[makeQuery(id+"F0.imprint","IMPRINT",EDGE,{"derivedFrom":sQuery(id+"F0.wireOp",EDGE,"E193")}),1.0]])]});
            var Q1;
            Q1=makeQuery(id+"F0.imprint","IMPRINT",FACE,{"disambiguationData":[TD([[makeQuery(id+"F0.imprint","IMPRINT",EDGE,{"derivedFrom":sQuery(id+"F0.wireOp",EDGE,"E0")}),1.0]])]});
            var Q2;
            Q2=makeQuery(id+"F0.imprint","IMPRINT",FACE,{"disambiguationData":[TD([[makeQuery(id+"F0.imprint","IMPRINT",EDGE,{"derivedFrom":sQuery(id+"F0.wireOp",EDGE,"E0")}),-1.0]])]});
            var Q3;
            Q3=makeQuery(id+"F0.imprint","IMPRINT",FACE,{"disambiguationData":[TD([[makeQuery(id+"F0.imprint","IMPRINT",EDGE,{"derivedFrom":sQuery(id+"F0.wireOp",EDGE,"E63")}),-1.0]])]});
            var Q4;
            Q4=makeQuery(id+"F0.imprint","IMPRINT",FACE,{"disambiguationData":[TD([[makeQuery(id+"F0.imprint","IMPRINT",EDGE,{"derivedFrom":sQuery(id+"F0.wireOp",EDGE,"E121")}),-1.0]])]});
            var Q5;
            Q5=makeQuery(id+"F0.imprint","IMPRINT",FACE,{"disambiguationData":[TD([[makeQuery(id+"F0.imprint","IMPRINT",EDGE,{"derivedFrom":sQuery(id+"F0.wireOp",EDGE,"E92")}),-1.0]])]});
            var Q6;
            Q6=makeQuery(id+"F0.imprint","IMPRINT",FACE,{"disambiguationData":[TD([[makeQuery(id+"F0.imprint","IMPRINT",EDGE,{"derivedFrom":sQuery(id+"F0.wireOp",EDGE,"E95")}),-1.0]])]});
            var Q7;
            Q7=makeQuery(id+"F0.imprint","IMPRINT",FACE,{"disambiguationData":[TD([[makeQuery(id+"F0.imprint","IMPRINT",EDGE,{"derivedFrom":sQuery(id+"F0.wireOp",EDGE,"E118")}),1.0]])]});
            var Q8;
            Q8=makeQuery(id+"F0.imprint","IMPRINT",FACE,{"disambiguationData":[TD([[makeQuery(id+"F0.imprint","IMPRINT",EDGE,{"derivedFrom":sQuery(id+"F0.wireOp",EDGE,"E48")}),-1.0]])]});
            var Q9;
            Q9=makeQuery(id+"F0.imprint","IMPRINT",FACE,{"disambiguationData":[TD([[makeQuery(id+"F0.imprint","IMPRINT",EDGE,{"derivedFrom":sQuery(id+"F0.wireOp",EDGE,"E42")}),-1.0]])]});
            var Q10;
            Q10=makeQuery(id+"F0.imprint","IMPRINT",FACE,{"disambiguationData":[TD([[makeQuery(id+"F0.imprint","IMPRINT",EDGE,{"derivedFrom":sQuery(id+"F0.wireOp",EDGE,"E58")}),1.0]])]});
            var Q11;
            Q11=makeQuery(id+"F0.imprint","IMPRINT",FACE,{"disambiguationData":[TD([[makeQuery(id+"F0.imprint","IMPRINT",EDGE,{"derivedFrom":sQuery(id+"F0.wireOp",EDGE,"E38")}),-1.0]])]});
            var Q12;
            Q12=makeQuery(id+"F0.imprint","IMPRINT",FACE,{"disambiguationData":[TD([[makeQuery(id+"F0.imprint","IMPRINT",EDGE,{"derivedFrom":sQuery(id+"F0.wireOp",EDGE,"E31")}),1.0]])]});
            var Q13;
            Q13=makeQuery(id+"F0.imprint","IMPRINT",FACE,{"disambiguationData":[TD([[makeQuery(id+"F0.imprint","IMPRINT",EDGE,{"derivedFrom":sQuery(id+"F0.wireOp",EDGE,"E26")}),1.0]])]});
            var Q14;
            Q14=makeQuery(id+"F0.imprint","IMPRINT",FACE,{"disambiguationData":[TD([[makeQuery(id+"F0.imprint","IMPRINT",EDGE,{"derivedFrom":sQuery(id+"F0.wireOp",EDGE,"E110")}),1.0]])]});
            var Q15;
            Q15=makeQuery(id+"F0.imprint","IMPRINT",FACE,{"disambiguationData":[TD([[makeQuery(id+"F0.imprint","IMPRINT",EDGE,{"derivedFrom":sQuery(id+"F0.wireOp",EDGE,"E129")}),-1.0]])]});
            var Q16;
            Q16=makeQuery(id+"F0.imprint","IMPRINT",FACE,{"disambiguationData":[TD([[makeQuery(id+"F0.imprint","IMPRINT",EDGE,{"derivedFrom":sQuery(id+"F0.wireOp",EDGE,"E137")}),-1.0]])]});
            var Q17;
            Q17=makeQuery(id+"F0.imprint","IMPRINT",FACE,{"disambiguationData":[TD([[makeQuery(id+"F0.imprint","IMPRINT",EDGE,{"derivedFrom":sQuery(id+"F0.wireOp",EDGE,"E160")}),-1.0]])]});
            var Q18;
            Q18=makeQuery(id+"F0.imprint","IMPRINT",FACE,{"disambiguationData":[TD([[makeQuery(id+"F0.imprint","IMPRINT",EDGE,{"derivedFrom":sQuery(id+"F0.wireOp",EDGE,"E22")}),1.0]])]});
            var Q19;
            Q19=makeQuery(id+"F0.imprint","IMPRINT",FACE,{"disambiguationData":[TD([[makeQuery(id+"F0.imprint","IMPRINT",EDGE,{"derivedFrom":sQuery(id+"F0.wireOp",EDGE,"E147")}),1.0]])]});
            var Q20;
            Q20=makeQuery(id+"F0.imprint","IMPRINT",FACE,{"disambiguationData":[TD([[makeQuery(id+"F0.imprint","IMPRINT",EDGE,{"derivedFrom":sQuery(id+"F0.wireOp",EDGE,"E140")}),1.0]])]});
            var Q21;
            Q21=makeQuery(id+"F0.imprint","IMPRINT",FACE,{"disambiguationData":[TD([[makeQuery(id+"F0.imprint","IMPRINT",EDGE,{"derivedFrom":sQuery(id+"F0.wireOp",EDGE,"E163")}),-1.0]])]});
            var Q22;
            Q22=makeQuery(id+"F0.imprint","IMPRINT",FACE,{"disambiguationData":[TD([[makeQuery(id+"F0.imprint","IMPRINT",EDGE,{"derivedFrom":sQuery(id+"F0.wireOp",EDGE,"8ccafac5-d668-442d-b003-5faf9abb5a7e")}),1.0]])]});
            var Q23;
            Q23=makeQuery(id+"F0.imprint","IMPRINT",FACE,{"disambiguationData":[TD([[makeQuery(id+"F0.imprint","IMPRINT",EDGE,{"derivedFrom":sQuery(id+"F0.wireOp",EDGE,"f306da12-e811-4d8b-8a4f-5ef17a733e3e")}),1.0]])]});
            extrude(context, id + "F3", {"entities" : qUnion([Q0, Q1, Q2, Q3, Q4, Q5, Q6, Q7, Q8, Q9, Q10, Q11, Q12, Q13, Q14, Q15, Q16, Q17, Q18, Q19, Q20, Q21, Q22, Q23]), "oppositeDirection" : true, "depth" : 5 * mm});
        }
    });
